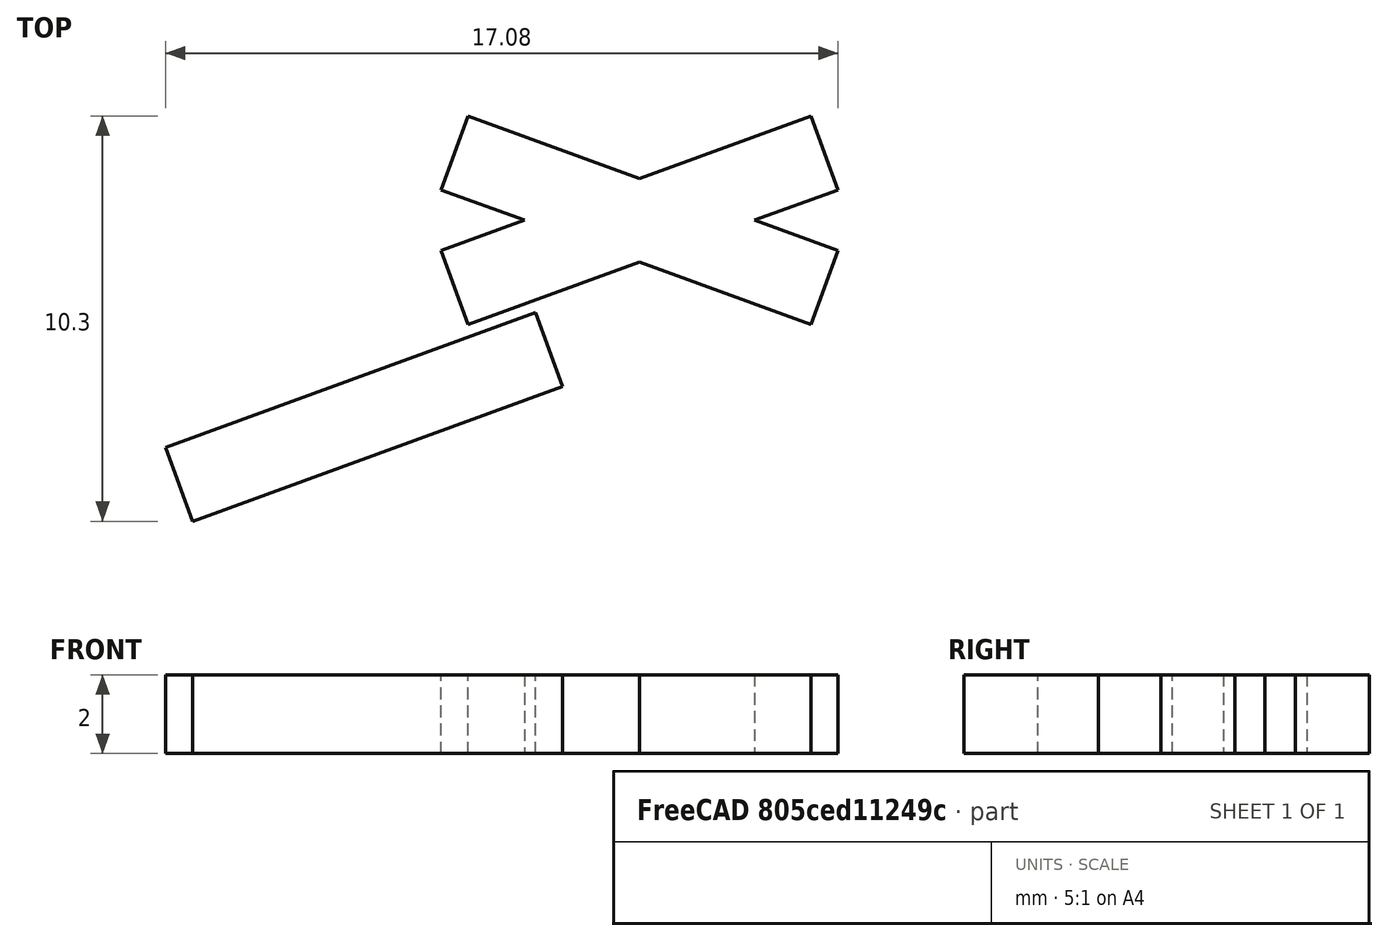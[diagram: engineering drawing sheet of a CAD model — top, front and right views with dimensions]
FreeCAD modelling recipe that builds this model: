
FCSTD DOCUMENT  (FreeCAD 1.0R39319 (Git))
Label: ojt1_t06_p01_
License: All rights reserved
LicenseURL: https://en.wikipedia.org/wiki/All_rights_reserved
objects: Part::Box×2, PartDesign::Boolean×1, PartDesign::Body×1
note: 5 computed .brp shape members not serialized (recipe doc carries the construction recipe); baked Part::Feature solids carry a one-line shape summary decoded from their .brp

FEATURE [Part::Box] Box  label="Cubo"
  AttacherType = Attacher::AttachEngine3D
  Height = 2
  Length = 10
  Placement = pos=(-5.04048,0.770408,0) rot=(0,0,4;5.93412rad)
  Width = 2
FEATURE [Part::Box] Box001  label="Cubo001"
  AttacherType = Attacher::AttachEngine3D
  Height = 2
  Length = 10
  Placement = pos=(-4.35644,-2.64979,0) rot=(0,0,4;0.349066rad)
  Width = 2
FEATURE [PartDesign::Boolean] Boolean
  Group = -> [Box,Box001]
  Refine = true
  Suppressed = false
  Type = 0
  UsePlacement = true
FEATURE [PartDesign::Body] Body
  AllowCompound = false
  Group = -> [Boolean]
  Origin = -> Origin
  Placement = pos=(7,5,0) rot=(0,0,1;0rad)
  Tip = -> Boolean
